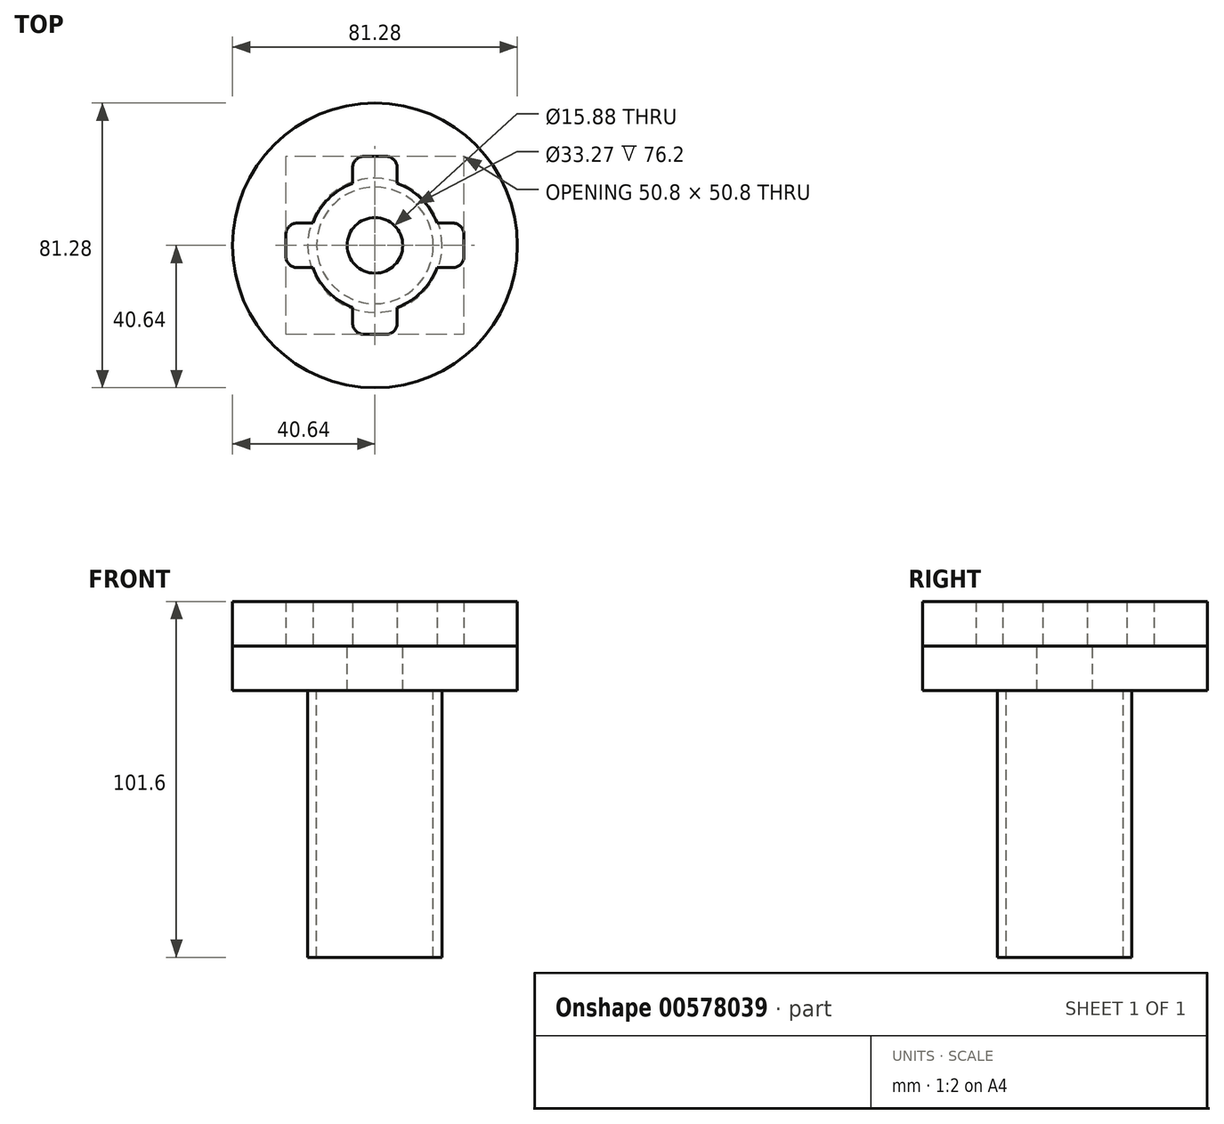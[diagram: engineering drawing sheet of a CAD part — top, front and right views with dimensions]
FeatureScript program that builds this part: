
annotation { "Feature Type Name" : "Feature", "Feature Type Description" : "" }
export const myFeature = defineFeature(function(context is Context, id is Id, definition is map)
    precondition{}
    {
        {
            var Q0;
            Q0=qCreatedBy(makeId("Top.planeOp"),FACE);
            var sketch = newSketch(context, id + "F0", { "sketchPlane" : qUnion([Q0])});
            skCircle(sketch, "E0", {"center": v(0, 0) * mm, "radius": 5.56 * mm});
            skCircle(sketch, "E1", {"center": v(0, 0) * mm, "radius": 7.94 * mm});
            skCircle(sketch, "E2", {"center": v(0, 0) * mm, "radius": 18.8 * mm});
            skLineSegment(sketch, "E3.bottom", {"start": v(22.23, -6.35) * mm, "end": v(17.7, -6.35) * mm});
            skLineSegment(sketch, "E3.top", {"start": v(22.23, 6.35) * mm, "end": v(17.7, 6.35) * mm});
            skLineSegment(sketch, "E3.left", {"start": v(25.4, -3.17) * mm, "end": v(25.4, 3.18) * mm});
            skLineSegment(sketch, "E3.right", {"start": v(-25.4, -3.18) * mm, "end": v(-25.4, 3.17) * mm});
            skPoint(sketch, "E4.visualSharp", {"position": v(-25.4, 6.35) * mm});
            skArc(sketch, "E4.filletArc", {"start": v(-22.23, 6.35) * mm, "mid": v(-24.47, 5.42) * mm, "end": v(-25.4, 3.17) * mm});
            skPoint(sketch, "E5.visualSharp", {"position": v(-25.4, -6.35) * mm});
            skArc(sketch, "E5.filletArc", {"start": v(-25.4, -3.18) * mm, "mid": v(-24.47, -5.42) * mm, "end": v(-22.23, -6.35) * mm});
            skPoint(sketch, "E6.visualSharp", {"position": v(25.4, -6.35) * mm});
            skArc(sketch, "E6.filletArc", {"start": v(22.23, -6.35) * mm, "mid": v(24.47, -5.42) * mm, "end": v(25.4, -3.17) * mm});
            skPoint(sketch, "E7.visualSharp", {"position": v(25.4, 6.35) * mm});
            skArc(sketch, "E7.filletArc", {"start": v(25.4, 3.18) * mm, "mid": v(24.47, 5.42) * mm, "end": v(22.23, 6.35) * mm});
            skPoint(sketch, "E8.1.0", {"position": v(-6.35, 25.4) * mm});
            skPoint(sketch, "E8.1.1", {"position": v(6.35, 25.4) * mm});
            skArc(sketch, "E8.1.2", {"start": v(-3.18, 25.4) * mm, "mid": v(-5.42, 24.47) * mm, "end": v(-6.35, 22.23) * mm});
            skArc(sketch, "E8.1.3", {"start": v(6.35, 22.23) * mm, "mid": v(5.42, 24.47) * mm, "end": v(3.17, 25.4) * mm});
            skLineSegment(sketch, "E8.1.4", {"start": v(-3.18, 25.4) * mm, "end": v(3.17, 25.4) * mm});
            skPoint(sketch, "E8.1.5", {"position": v(-6.35, -25.4) * mm});
            skLineSegment(sketch, "E8.1.6", {"start": v(-3.17, -25.4) * mm, "end": v(3.18, -25.4) * mm});
            skArc(sketch, "E8.1.7", {"start": v(-6.35, -22.23) * mm, "mid": v(-5.42, -24.47) * mm, "end": v(-3.17, -25.4) * mm});
            skArc(sketch, "E8.1.8", {"start": v(3.18, -25.4) * mm, "mid": v(5.42, -24.47) * mm, "end": v(6.35, -22.23) * mm});
            skPoint(sketch, "E8.1.9", {"position": v(6.35, -25.4) * mm});
            skLineSegment(sketch, "E8.1.10", {"start": v(-6.35, -22.23) * mm, "end": v(-6.35, -17.7) * mm});
            skLineSegment(sketch, "E8.1.11", {"start": v(6.35, -22.23) * mm, "end": v(6.35, -17.7) * mm});
            skLineSegment(sketch, "E8.anchor1", {"start": v(0, 0) * mm, "end": v(-25.4, -6.35) * mm, "construction": true});
            skLineSegment(sketch, "E8.anchor2", {"start": v(0, 0) * mm, "end": v(-6.35, 25.4) * mm, "construction": true});
            skLineSegment(sketch, "E9.trimOffspring", {"start": v(-6.35, 17.7) * mm, "end": v(-6.35, 22.23) * mm});
            skLineSegment(sketch, "E10.trimOffspring", {"start": v(-17.7, 6.35) * mm, "end": v(-22.23, 6.35) * mm});
            skLineSegment(sketch, "E11.trimOffspring", {"start": v(-17.7, -6.35) * mm, "end": v(-22.23, -6.35) * mm});
            skLineSegment(sketch, "E12.trimOffspring", {"start": v(6.35, 17.7) * mm, "end": v(6.35, 22.23) * mm});
            skCircle(sketch, "E13", {"center": v(0, 0) * mm, "radius": 40.64 * mm});
            skCircle(sketch, "E14.0", {"center": v(0, 0) * mm, "radius": 7.84 * mm});
            skSolve(sketch);
        }
        {
            var Q0;
            {var subQ2=sQuery(id+"F0.wireOp",EDGE,"E3.bottom");Q0=makeQuery(id+"F0.imprint","IMPRINT",FACE,{"disambiguationData":[TD([[makeQuery(id+"F0.imprint","IMPRINT",EDGE,{"derivedFrom":subQ2}),1.0]])]});}
            extrude(context, id + "F1", {"entities" : qUnion([Q0]), "depth" : 12.7 * mm, "offsetDistance" : 25.4 * mm});
        }
        {
            var Q0;
            Q0=makeQuery(id+"F0.imprint","IMPRINT",FACE,{"disambiguationData":[TD([[makeQuery(id+"F0.imprint","IMPRINT",EDGE,{"derivedFrom":sQuery(id+"F0.wireOp",EDGE,"E3.right")}),-1.0]])]});
            var Q1;
            Q1=makeQuery(id+"F0.imprint","IMPRINT",FACE,{"disambiguationData":[TD([[makeQuery(id+"F0.imprint","IMPRINT",EDGE,{"derivedFrom":sQuery(id+"F0.wireOp",EDGE,"E1")}),-1.0]])]});
            var Q2;
            {var subQ2=sQuery(id+"F0.wireOp",EDGE,"E3.bottom");Q2=makeQuery(id+"F0.imprint","IMPRINT",FACE,{"disambiguationData":[TD([[makeQuery(id+"F0.imprint","IMPRINT",EDGE,{"derivedFrom":subQ2}),1.0]])]});}
            var Q3;
            {var subQ1=sQuery(id+"F0.wireOp",EDGE,"E3.bottom");Q3=makeQuery(id+"F0.imprint","IMPRINT",FACE,{"disambiguationData":[TD([[makeQuery(id+"F0.imprint","IMPRINT",EDGE,{"derivedFrom":subQ1}),-1.0]])]});}
            var Q4;
            Q4 = qSketchRegion(id + "F0", true);
            var Q5;
            Q5=makeQuery(id+"F0.imprint","IMPRINT",FACE,{"disambiguationData":[TD([[makeQuery(id+"F0.imprint","IMPRINT",EDGE,{"derivedFrom":sQuery(id+"F0.wireOp",EDGE,"E8.1.6")}),1.0]])]});
            var Q6;
            Q6=makeQuery(id+"F0.imprint","IMPRINT",FACE,{"disambiguationData":[TD([[makeQuery(id+"F0.imprint","IMPRINT",EDGE,{"derivedFrom":sQuery(id+"F0.wireOp",EDGE,"E8.1.2")}),1.0]])]});
            extrude(context, id + "F2", {"entities" : qUnion([Q0, Q1, Q2, Q3, Q4, Q5, Q6]), "oppositeDirection" : true, "depth" : 12.7 * mm, "offsetDistance" : 25.4 * mm});
        }
        {
            var Q0;
            Q0=makeQuery(id+"F2.opExtrude","CAP_FACE",FACE,{"disambiguationData":[OSD([sQuery(id+"F0.wireOp",EDGE,"E1"),sQuery(id+"F0.wireOp",EDGE,"E13")])],"isStart":false});
            var sketch = newSketch(context, id + "F3", { "sketchPlane" : qUnion([Q0])});
            skCircle(sketch, "E15", {"center": v(0, 0) * mm, "radius": 16.64 * mm});
            skCircle(sketch, "E16.0", {"center": v(0, 0) * mm, "radius": 19.18 * mm});
            skCircle(sketch, "E17.0", {"center": v(0, 0) * mm, "radius": 34.3 * mm});
            skSolve(sketch);
        }
        {
            var Q0;
            Q0=makeQuery(id+"F3.imprint","IMPRINT",FACE,{"disambiguationData":[TD([[makeQuery(id+"F3.imprint","IMPRINT",EDGE,{"derivedFrom":sQuery(id+"F3.wireOp",EDGE,"E15")}),-1.0]])]});
            extrude(context, id + "F4", {"entities" : qUnion([Q0]), "operationType" : NewBodyOperationType.ADD, "depth" : 76.2 * mm, "offsetDistance" : 25.4 * mm});
        }
    });
